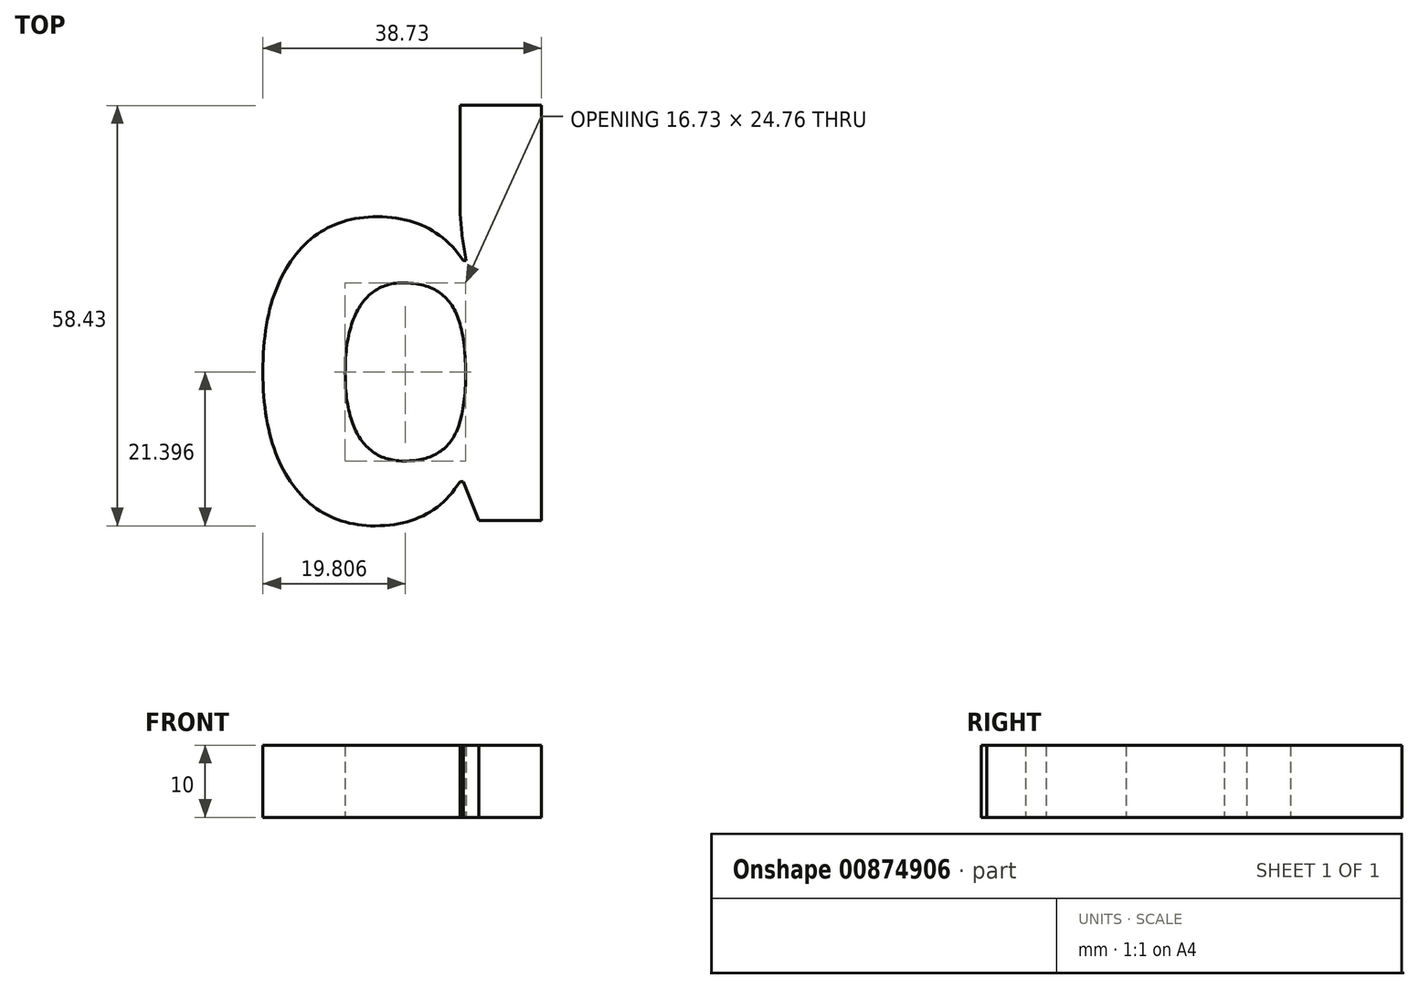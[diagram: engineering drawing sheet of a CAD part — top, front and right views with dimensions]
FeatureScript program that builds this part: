
annotation { "Feature Type Name" : "Feature", "Feature Type Description" : "" }
export const myFeature = defineFeature(function(context is Context, id is Id, definition is map)
    precondition{}
    {
        {
            var Q0;
            Q0=qCreatedBy(makeId("Top.planeOp"),FACE);
            var sketch = newSketch(context, id + "F0", { "sketchPlane" : qUnion([Q0])});
            skText(sketch, "E0", { "text": "d", "fontName": "OpenSans-Bold.ttf"});
            const initialGuessF0  = {"E0": [0, 0, 1, 0, 0.05466]};
            skSetInitialGuess(sketch, initialGuessF0);
            skSolve(sketch);
        }
        {
            var Q0;
            Q0 = qSketchRegion(id + "F0", true);
            extrude(context, id + "F1", {"entities" : qUnion([Q0]), "depth" : 10 * mm, "offsetDistance" : 25 * mm});
        }
    });
